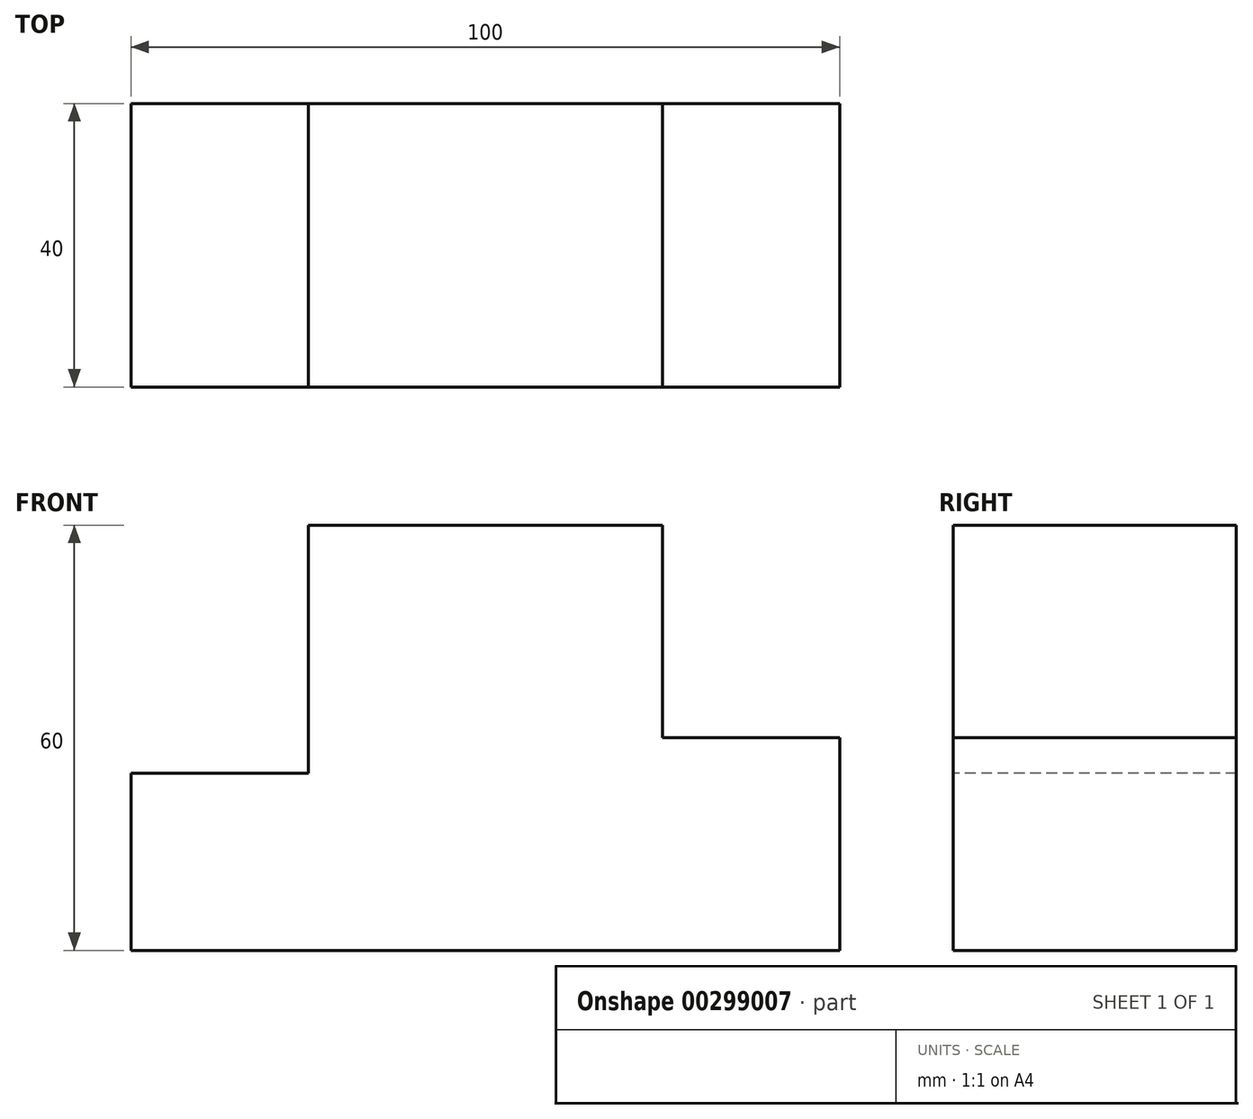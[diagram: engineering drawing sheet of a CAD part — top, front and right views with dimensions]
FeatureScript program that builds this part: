
annotation { "Feature Type Name" : "Feature", "Feature Type Description" : "" }
export const myFeature = defineFeature(function(context is Context, id is Id, definition is map)
    precondition{}
    {
        {
            var Q0;
            Q0=qCreatedBy(makeId("Front.planeOp"),FACE);
            var sketch = newSketch(context, id + "F0", { "sketchPlane" : qUnion([Q0])});
            skLineSegment(sketch, "E0.bottom", {"start": v(50, -30) * mm, "end": v(-50, -30) * mm});
            skLineSegment(sketch, "E0.top", {"start": v(50, 30) * mm, "end": v(-50, 30) * mm});
            skLineSegment(sketch, "E0.left", {"start": v(50, -30) * mm, "end": v(50, 30) * mm});
            skLineSegment(sketch, "E0.right", {"start": v(-50, -30) * mm, "end": v(-50, 30) * mm});
            skPoint(sketch, "E0.middle", {"position": v(0, 0) * mm});
            skSolve(sketch);
        }
        {
            var Q0;
            Q0 = qSketchRegion(id + "F0", true);
            extrude(context, id + "F1", {"entities" : qUnion([Q0]), "depth" : 40 * mm});
        }
        {
            var Q0;
            Q0=makeQuery(id+"F1.opExtrude","CAP_FACE",FACE,{"disambiguationData":[OSD([sQuery(id+"F0.wireOp",EDGE,"E0.bottom"),sQuery(id+"F0.wireOp",EDGE,"E0.top"),sQuery(id+"F0.wireOp",EDGE,"E0.left"),sQuery(id+"F0.wireOp",EDGE,"E0.right")])],"isStart":false});
            var sketch = newSketch(context, id + "F2", { "sketchPlane" : qUnion([Q0])});
            skLineSegment(sketch, "E1.bottom", {"start": v(-50, 30) * mm, "end": v(-25, 30) * mm});
            skLineSegment(sketch, "E1.top", {"start": v(-50, -5) * mm, "end": v(-25, -5) * mm});
            skLineSegment(sketch, "E1.left", {"start": v(-50, 30) * mm, "end": v(-50, -5) * mm});
            skLineSegment(sketch, "E1.right", {"start": v(-25, 30) * mm, "end": v(-25, -5) * mm});
            skSolve(sketch);
        }
        {
            var Q0;
            Q0 = qSketchRegion(id + "F2", true);
            extrude(context, id + "F3", {"entities" : qUnion([Q0]), "operationType" : NewBodyOperationType.REMOVE, "oppositeDirection" : true, "depth" : 54 * mm});
        }
        {
            var Q0;
            Q0=makeQuery(id+"F1.opExtrude","CAP_FACE",FACE,{"disambiguationData":[OSD([sQuery(id+"F0.wireOp",EDGE,"E0.bottom"),sQuery(id+"F0.wireOp",EDGE,"E0.top"),sQuery(id+"F0.wireOp",EDGE,"E0.left"),sQuery(id+"F0.wireOp",EDGE,"E0.right")])],"isStart":false});
            var sketch = newSketch(context, id + "F4", { "sketchPlane" : qUnion([Q0])});
            skLineSegment(sketch, "E2.bottom", {"start": v(50, 30) * mm, "end": v(25, 30) * mm});
            skLineSegment(sketch, "E2.top", {"start": v(50, 0) * mm, "end": v(25, 0) * mm});
            skLineSegment(sketch, "E2.left", {"start": v(50, 30) * mm, "end": v(50, 0) * mm});
            skLineSegment(sketch, "E2.right", {"start": v(25, 30) * mm, "end": v(25, 0) * mm});
            skSolve(sketch);
        }
        {
            var Q0;
            Q0=makeQuery(id+"F4.imprint","IMPRINT",FACE,{"disambiguationData":[TD([[makeQuery(id+"F4.imprint","IMPRINT",EDGE,{"derivedFrom":sQuery(id+"F4.wireOp",EDGE,"E2.bottom")}),1.0]])]});
            extrude(context, id + "F5", {"entities" : qUnion([Q0]), "operationType" : NewBodyOperationType.REMOVE, "oppositeDirection" : true, "depth" : 60 * mm});
        }
    });
